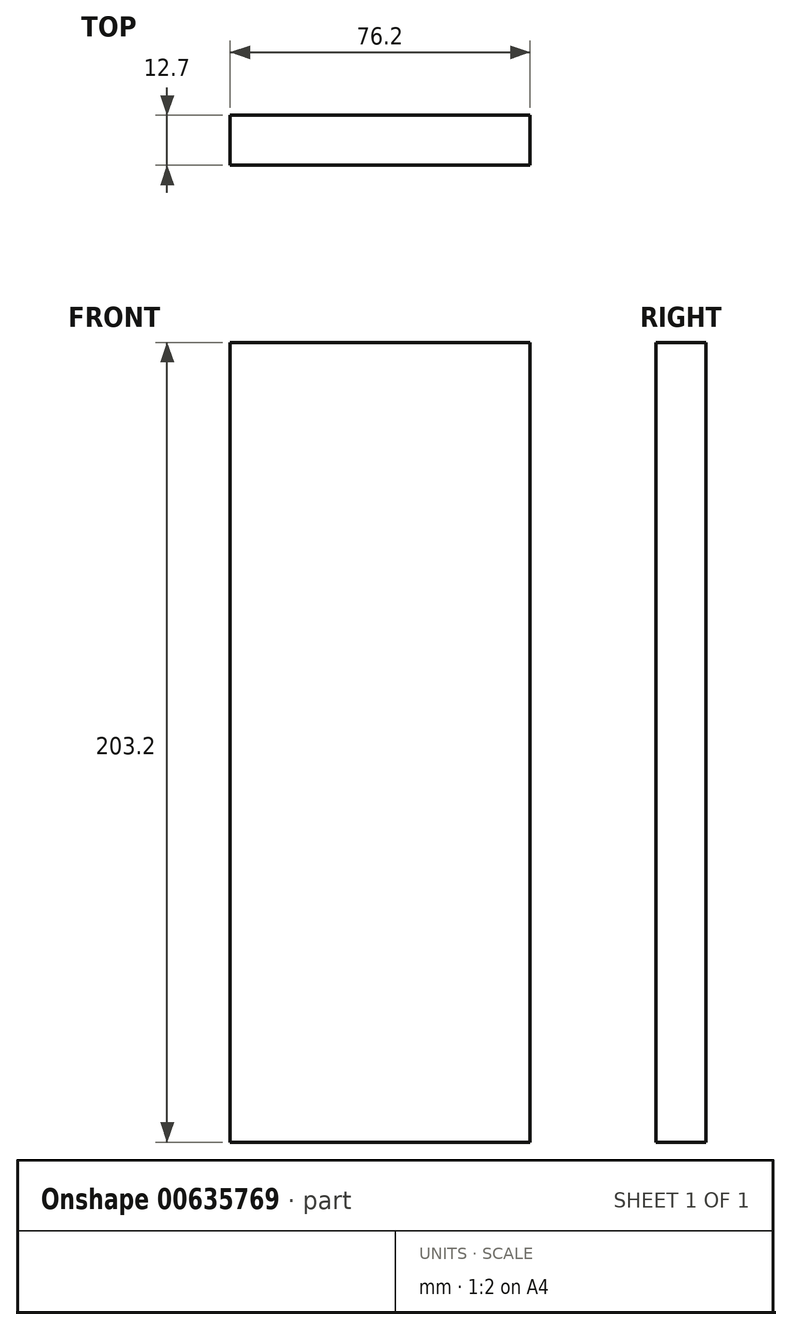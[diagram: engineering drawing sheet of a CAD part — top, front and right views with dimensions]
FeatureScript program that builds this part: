
annotation { "Feature Type Name" : "Feature", "Feature Type Description" : "" }
export const myFeature = defineFeature(function(context is Context, id is Id, definition is map)
    precondition{}
    {
        {
            var Q0;
            Q0=qCreatedBy(makeId("Front.planeOp"),FACE);
            var sketch = newSketch(context, id + "F0", { "sketchPlane" : qUnion([Q0])});
            skLineSegment(sketch, "E0.bottom", {"start": v(38.1, -101.6) * mm, "end": v(-38.1, -101.6) * mm});
            skLineSegment(sketch, "E0.top", {"start": v(38.1, 101.6) * mm, "end": v(-38.1, 101.6) * mm});
            skLineSegment(sketch, "E0.left", {"start": v(38.1, -101.6) * mm, "end": v(38.1, 101.6) * mm});
            skLineSegment(sketch, "E0.right", {"start": v(-38.1, -101.6) * mm, "end": v(-38.1, 101.6) * mm});
            skPoint(sketch, "E0.middle", {"position": v(0, 0) * mm});
            skSolve(sketch);
        }
        {
            var Q0;
            Q0=makeQuery(id+"F0.imprint","IMPRINT",FACE,{"disambiguationData":[TD([[makeQuery(id+"F0.imprint","IMPRINT",EDGE,{"derivedFrom":sQuery(id+"F0.wireOp",EDGE,"E0.bottom")}),-1.0]])]});
            extrude(context, id + "F1", {"entities" : qUnion([Q0]), "endBound" : BoundingType.SYMMETRIC, "depth" : 12.7 * mm, "offsetDistance" : 25.4 * mm});
        }
    });
